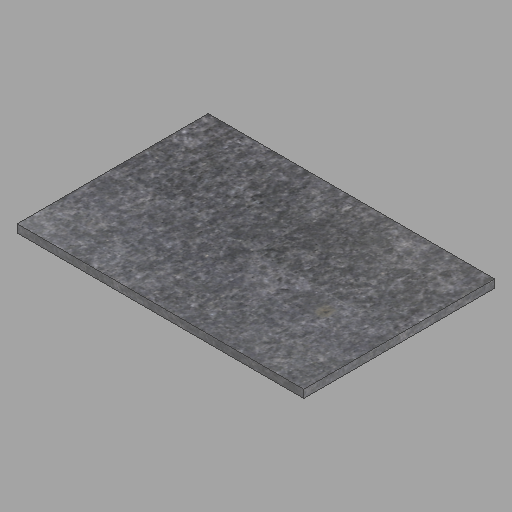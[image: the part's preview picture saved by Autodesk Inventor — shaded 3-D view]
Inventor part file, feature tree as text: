
AUTODESK INVENTOR PART (.ipt)
format: ipt  version: 2023 (Build 270158000, 158)  size: 229,376 bytes
history: native  units: in
note: dims shown in document units (in); Inventor stores cm internally (conversion verified against a paired STEP export)
features: other x1, extrude x1, sketch x1
ambient origin geometry x8: Origin, YZ Plane, XZ Plane, XY Plane, X Axis, Y Axis, Z Axis, Center Point
bodies: Body1 (feature_tree)
feature tree (3):
  other  "24x36x2-50"
  extrude  "Extrusion2"  Depth=24.0in
  sketch  "Sketch3"  dims[d4=36.0in d5=24.0in d6=1.0in d7=0.0in]
